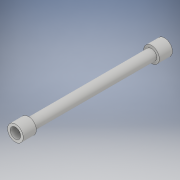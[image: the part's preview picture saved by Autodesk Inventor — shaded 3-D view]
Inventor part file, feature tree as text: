
AUTODESK INVENTOR PART (.ipt)
format: ipt  version: 2018 (Build 220112000, 112)  size: 114,688 bytes
history: native  units: in
note: dims shown in document units (in); Inventor stores cm internally (conversion verified against a paired STEP export)
features: extrude x5, sketch x4
ambient origin geometry x8: Origin, YZ Plane, XZ Plane, XY Plane, X Axis, Y Axis, Z Axis, Center Point
bodies: Solid1 (feature_tree)
feature tree (9):
  extrude  "Extrusion1"  Depth=1.8504in TaperAngle=0.0deg
  sketch  "Sketch2"  dims[d3=0.2362in d4=0.1969in d5=0.0in]
  extrude  "Extrusion2"  Depth=0.1969in TaperAngle=0.0deg
  extrude  "Extrusion3"  Depth=0.1969in TaperAngle=0.0deg
  extrude  "Extrusion4"  Depth=0.1181in TaperAngle=0.0deg
  extrude  "Extrusion5"  [1 undecoded]
  sketch  "Sketch1"  dims[d0=0.1575in d1=1.8504in d2=0.0in]
  sketch  "Sketch3"  dims[d6=0.0787in d7=0.0in d8=0.1969in d9=0.0in]
  sketch  "Sketch4"  dims[d10=0.1575in d11=0.1181in d12=0.0in]
note: 1 required parameter value undecoded (feature->parameter linkage not recoverable at this tier; creation-order binding heuristic only, values carry confidence <= 0.55)
